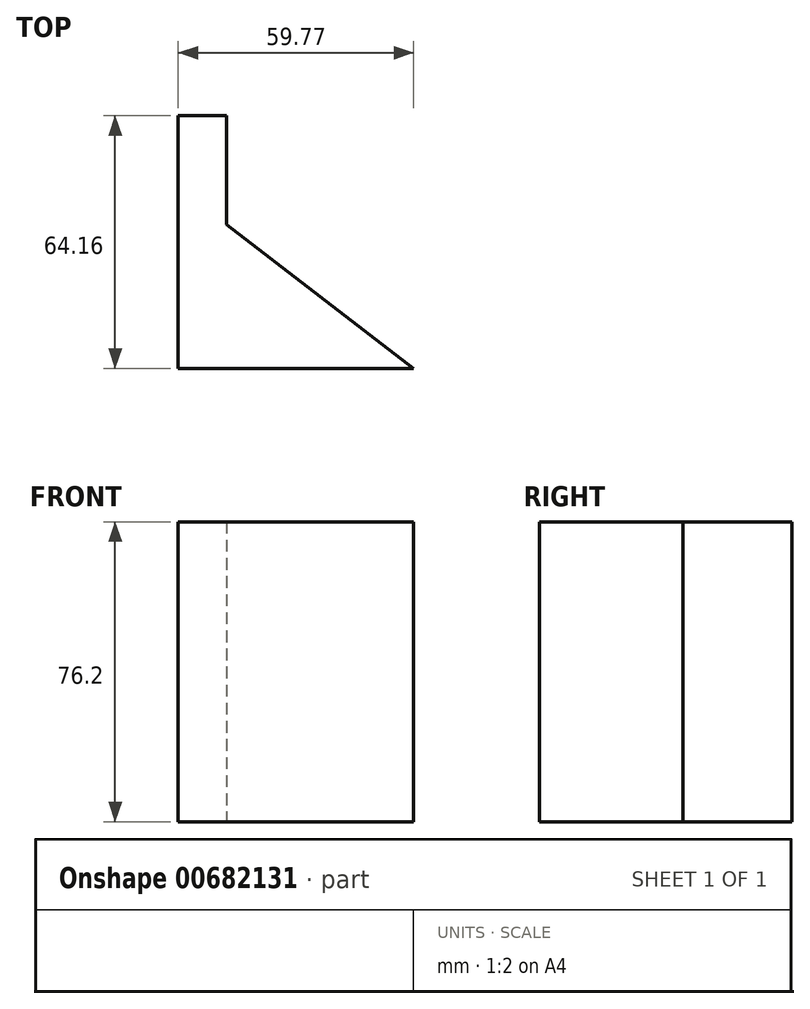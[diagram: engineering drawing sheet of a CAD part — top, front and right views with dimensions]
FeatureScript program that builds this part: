
annotation { "Feature Type Name" : "Feature", "Feature Type Description" : "" }
export const myFeature = defineFeature(function(context is Context, id is Id, definition is map)
    precondition{}
    {
        {
            var Q0;
            Q0=qCreatedBy(makeId("Top.planeOp"),FACE);
            var sketch = newSketch(context, id + "F0", { "sketchPlane" : qUnion([Q0])});
            skLineSegment(sketch, "E0", {"start": v(-53.18, 37.9) * mm, "end": v(-53.18, -26.26) * mm});
            skLineSegment(sketch, "E1", {"start": v(-53.18, -26.26) * mm, "end": v(6.59, -26.26) * mm});
            skLineSegment(sketch, "E2", {"start": v(6.59, -26.26) * mm, "end": v(-40.96, 10.22) * mm});
            skLineSegment(sketch, "E3", {"start": v(-40.96, 10.22) * mm, "end": v(-40.96, 37.9) * mm});
            skLineSegment(sketch, "E4", {"start": v(-40.96, 37.9) * mm, "end": v(-53.18, 37.9) * mm});
            skSolve(sketch);
        }
        {
            var Q0;
            Q0 = qSketchRegion(id + "F0", true);
            extrude(context, id + "F1", {"entities" : qUnion([Q0]), "depth" : 76.2 * mm, "offsetDistance" : 25.4 * mm});
        }
    });
